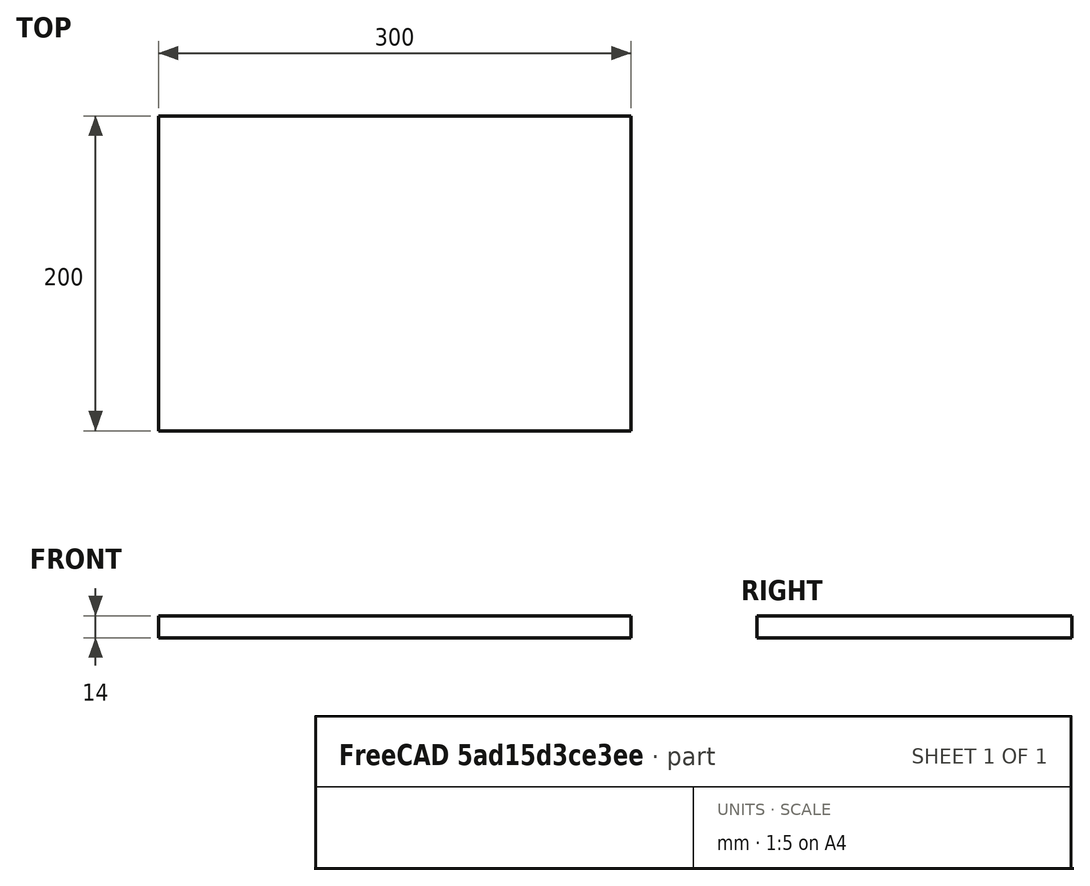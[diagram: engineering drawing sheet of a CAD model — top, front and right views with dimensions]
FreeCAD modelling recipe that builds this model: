
FCSTD DOCUMENT  (FreeCAD 0.19R24276 (Git))
Label: plastina_200x300_v1
License: All rights reserved
LicenseURL: http://en.wikipedia.org/wiki/All_rights_reserved
objects: Sketcher::SketchObject×1, PartDesign::Pad×1, PartDesign::Body×1
note: 4 computed .brp shape members not serialized (recipe doc carries the construction recipe); baked Part::Feature solids carry a one-line shape summary decoded from their .brp

FEATURE [Sketcher::SketchObject] Sketch
  FullyConstrained = true
  MapMode = 5
  Support = -> [XY_Plane]
  sketch-geometry (4):
    g0: LineSegment StartX=0 StartY=0 StartZ=0 EndX=300 EndY=0 EndZ=0
    g1: LineSegment StartX=300 StartY=0 StartZ=0 EndX=300 EndY=200 EndZ=0
    g2: LineSegment StartX=300 StartY=200 StartZ=0 EndX=0 EndY=200 EndZ=0
    g3: LineSegment StartX=0 StartY=200 StartZ=0 EndX=0 EndY=0 EndZ=0
  constraints (11):
    c: Coincident(g0,g1)
    c: Coincident(g1,g2)
    c: Coincident(g2,g3)
    c: Coincident(g3,g0)
    c: Horizontal(g0)
    c: Horizontal(g2)
    c: Vertical(g1)
    c: Vertical(g3)
    c: Coincident(g0,g-1)
    c: DistanceY(g1,g1) = 200
    c: DistanceX(g0,g0) = 300
FEATURE [PartDesign::Pad] Pad
  Direction = (1,1,1)
  Length = 14
  Length2 = 100
  Profile = -> Sketch
  Type = 0
FEATURE [PartDesign::Body] Body
  Group = -> [Sketch,Pad]
  Origin = -> Origin
  Tip = -> Pad
